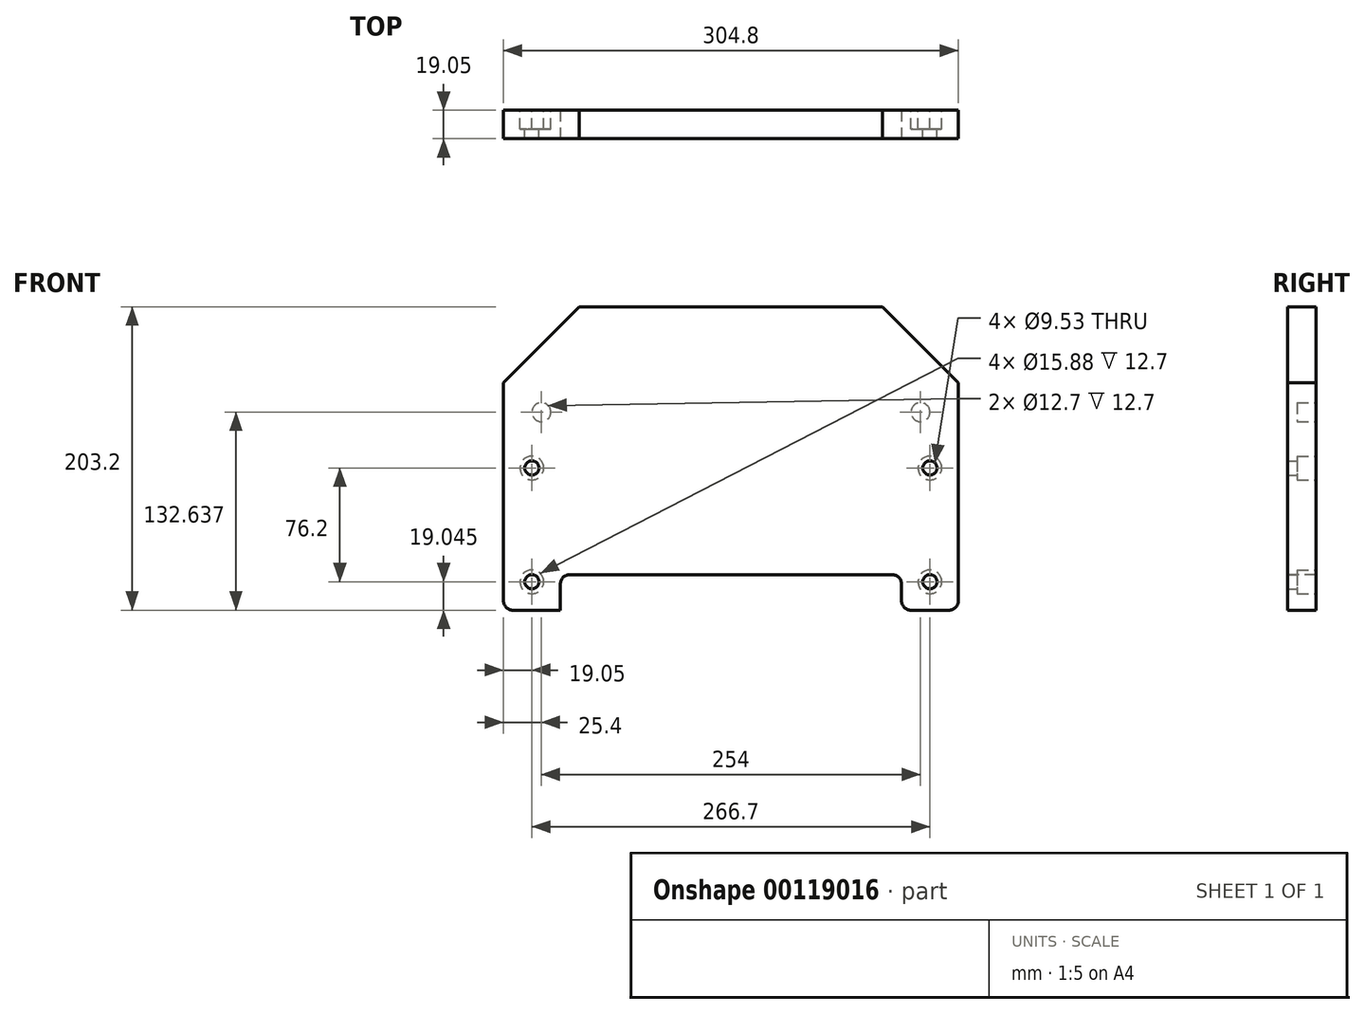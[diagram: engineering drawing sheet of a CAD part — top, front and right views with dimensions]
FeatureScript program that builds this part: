
annotation { "Feature Type Name" : "Feature", "Feature Type Description" : "" }
export const myFeature = defineFeature(function(context is Context, id is Id, definition is map)
    precondition{}
    {
        {
            var Q0;
            Q0=qCreatedBy(makeId("Front.planeOp"),FACE);
            var sketch = newSketch(context, id + "F0", { "sketchPlane" : qUnion([Q0])});
            skLineSegment(sketch, "E0.bottom", {"start": v(-194.83, 94.03) * mm, "end": v(109.97, 94.03) * mm});
            skLineSegment(sketch, "E0.top", {"start": v(-194.83, -109.17) * mm, "end": v(109.97, -109.17) * mm});
            skLineSegment(sketch, "E0.left", {"start": v(-194.83, 94.03) * mm, "end": v(-194.83, -109.17) * mm});
            skLineSegment(sketch, "E0.right", {"start": v(109.97, 94.03) * mm, "end": v(109.97, -109.17) * mm});
            skSolve(sketch);
        }
        {
            var Q0;
            Q0=makeQuery(id+"F0.imprint","IMPRINT",FACE,{"disambiguationData":[TD([[makeQuery(id+"F0.imprint","IMPRINT",EDGE,{"derivedFrom":sQuery(id+"F0.wireOp",EDGE,"E0.bottom")}),-1.0]])]});
            extrude(context, id + "F1", {"entities" : qUnion([Q0]), "depth" : 19.05 * mm});
        }
        {
            var Q0;
            Q0=makeQuery(id+"F1.opExtrude","CAP_FACE",FACE,{"disambiguationData":[OSD([sQuery(id+"F0.wireOp",EDGE,"E0.bottom"),sQuery(id+"F0.wireOp",EDGE,"E0.top"),sQuery(id+"F0.wireOp",EDGE,"E0.left"),sQuery(id+"F0.wireOp",EDGE,"E0.right")])],"isStart":false});
            var sketch = newSketch(context, id + "F2", { "sketchPlane" : qUnion([Q0])});
            skLineSegment(sketch, "E1.bottom", {"start": v(-156.73, -109.17) * mm, "end": v(71.87, -109.17) * mm});
            skLineSegment(sketch, "E1.top", {"start": v(-156.73, -85.32) * mm, "end": v(71.87, -85.32) * mm});
            skLineSegment(sketch, "E1.left", {"start": v(-156.73, -109.17) * mm, "end": v(-156.73, -85.32) * mm});
            skLineSegment(sketch, "E1.right", {"start": v(71.87, -109.17) * mm, "end": v(71.87, -85.32) * mm});
            skSolve(sketch);
        }
        {
            var Q0;
            Q0 = qSketchRegion(id + "F2", true);
            extrude(context, id + "F3", {"entities" : qUnion([Q0]), "operationType" : NewBodyOperationType.REMOVE, "endBound" : BoundingType.THROUGH_ALL, "oppositeDirection" : true, "depth" : 25.4 * mm});
        }
        {
            var Q0;
            Q0=makeQuery(id+"F3.boolean.opBoolean","COPY",EDGE,{"derivedFrom":makeQuery(id+"F3.opExtrude","SWEPT_EDGE",EDGE,{"disambiguationData":[OSD([sQuery(id+"F2.wireOp",EDGE,"E1.top"),sQuery(id+"F2.wireOp",EDGE,"E1.left")])]})});
            var Q1;
            Q1=makeQuery(id+"F3.boolean.opBoolean","COPY",EDGE,{"derivedFrom":makeQuery(id+"F3.opExtrude","SWEPT_EDGE",EDGE,{"disambiguationData":[OSD([sQuery(id+"F0.wireOp",EDGE,"E0.top"),sQuery(id+"F2.wireOp",EDGE,"E1.bottom"),sQuery(id+"F2.wireOp",EDGE,"E1.left")])]})});
            var Q2;
            Q2=makeQuery(id+"F1.opExtrude","SWEPT_EDGE",EDGE,{"disambiguationData":[OSD([sQuery(id+"F0.wireOp",EDGE,"E0.top"),sQuery(id+"F0.wireOp",EDGE,"E0.left")])]});
            var Q3;
            Q3=makeQuery(id+"F3.boolean.opBoolean","COPY",EDGE,{"derivedFrom":makeQuery(id+"F3.opExtrude","SWEPT_EDGE",EDGE,{"disambiguationData":[OSD([sQuery(id+"F2.wireOp",EDGE,"E1.top"),sQuery(id+"F2.wireOp",EDGE,"E1.right")])]})});
            var Q4;
            Q4=makeQuery(id+"F3.boolean.opBoolean","COPY",EDGE,{"derivedFrom":makeQuery(id+"F3.opExtrude","SWEPT_EDGE",EDGE,{"disambiguationData":[OSD([sQuery(id+"F0.wireOp",EDGE,"E0.top"),sQuery(id+"F2.wireOp",EDGE,"E1.bottom"),sQuery(id+"F2.wireOp",EDGE,"E1.right")])]})});
            var Q5;
            Q5=makeQuery(id+"F1.opExtrude","SWEPT_EDGE",EDGE,{"disambiguationData":[OSD([sQuery(id+"F0.wireOp",EDGE,"E0.top"),sQuery(id+"F0.wireOp",EDGE,"E0.right")])]});
            fillet(context, id + "F4", {"entities" : qUnion([Q0, Q1, Q2, Q3, Q4, Q5]), "radius" : 6.35 * mm, "tangentPropagation" : true, "allowEdgeOverflow" : false});
        }
        {
            var Q0;
            Q0=makeQuery(id+"F1.opExtrude","CAP_FACE",FACE,{"disambiguationData":[OSD([sQuery(id+"F0.wireOp",EDGE,"E0.bottom"),sQuery(id+"F0.wireOp",EDGE,"E0.top"),sQuery(id+"F0.wireOp",EDGE,"E0.left"),sQuery(id+"F0.wireOp",EDGE,"E0.right")])],"isStart":true});
            var sketch = newSketch(context, id + "F5", { "sketchPlane" : qUnion([Q0])});
            skPoint(sketch, "E2", {"position": v(42.43, -5.1) * mm});
            skPoint(sketch, "E2.positionSnap0", {"position": v(42.43, -85.32) * mm});
            skLineSegment(sketch, "E3", {"start": v(42.43, -5.1) * mm, "end": v(42.43, 23.47) * mm, "construction": true});
            skLineSegment(sketch, "E4", {"start": v(42.43, 23.47) * mm, "end": v(-84.57, 23.47) * mm});
            skLineSegment(sketch, "E5", {"start": v(42.43, 23.47) * mm, "end": v(169.43, 23.47) * mm});
            skCircle(sketch, "E6", {"center": v(169.43, 23.47) * mm, "radius": 6.35 * mm});
            skCircle(sketch, "E7", {"center": v(-84.57, 23.47) * mm, "radius": 6.35 * mm});
            skSolve(sketch);
        }
        {
            var Q0;
            Q0 = qSketchRegion(id + "F5", true);
            extrude(context, id + "F6", {"entities" : qUnion([Q0]), "operationType" : NewBodyOperationType.REMOVE, "oppositeDirection" : true, "depth" : 12.7 * mm});
        }
        {
            var Q0;
            Q0=makeQuery(id+"F1.opExtrude","CAP_FACE",FACE,{"disambiguationData":[OSD([sQuery(id+"F0.wireOp",EDGE,"E0.bottom"),sQuery(id+"F0.wireOp",EDGE,"E0.top"),sQuery(id+"F0.wireOp",EDGE,"E0.left"),sQuery(id+"F0.wireOp",EDGE,"E0.right")])],"isStart":true});
            var sketch = newSketch(context, id + "F7", { "sketchPlane" : qUnion([Q0])});
            skPoint(sketch, "E8", {"position": v(-90.92, -90.12) * mm});
            skPoint(sketch, "E8.positionSnap0", {"position": v(-90.92, -109.17) * mm});
            skPoint(sketch, "E9", {"position": v(-90.92, -13.92) * mm});
            skPoint(sketch, "E10", {"position": v(175.78, -90.12) * mm});
            skPoint(sketch, "E10.positionSnap0", {"position": v(175.78, -109.17) * mm});
            skPoint(sketch, "E11", {"position": v(175.78, -13.92) * mm});
            skSolve(sketch);
        }
        {
            var Q0;
            Q0=sQuery(id+"F7.wireOp",VERTEX,"E9");
            var Q1;
            Q1=sQuery(id+"F7.wireOp",VERTEX,"E8");
            var Q2;
            Q2=sQuery(id+"F7.wireOp",VERTEX,"E10");
            var Q3;
            Q3=sQuery(id+"F7.wireOp",VERTEX,"E11");
            var Q4;
            Q4=makeQuery(id+"F1.opExtrude","SWEPT_BODY",BODY,{"disambiguationData":[OSD([sQuery(id+"F0.wireOp",EDGE,"E0.bottom"),sQuery(id+"F0.wireOp",EDGE,"E0.top"),sQuery(id+"F0.wireOp",EDGE,"E0.left"),sQuery(id+"F0.wireOp",EDGE,"E0.right")])]});
            hole(context, id + "F8", {"style" : HoleStyle.C_BORE, "endStyle" : HoleEndStyle.THROUGH, "holeDiameter" : 9.52 * mm, "cBoreDiameter" : 15.88 * mm, "cBoreDepth" : 12.7 * mm, "locations" : qUnion([Q0, Q1, Q2, Q3]), "scope" : qUnion([Q4]), "isTappedThrough" : true});
        }
        {
            var Q0;
            Q0=makeQuery(id+"F1.opExtrude","SWEPT_EDGE",EDGE,{"disambiguationData":[OSD([sQuery(id+"F0.wireOp",EDGE,"E0.bottom"),sQuery(id+"F0.wireOp",EDGE,"E0.right")])]});
            var Q1;
            Q1=makeQuery(id+"F1.opExtrude","SWEPT_EDGE",EDGE,{"disambiguationData":[OSD([sQuery(id+"F0.wireOp",EDGE,"E0.bottom"),sQuery(id+"F0.wireOp",EDGE,"E0.left")])]});
            chamfer(context, id + "F9", {"entities" : qUnion([Q0, Q1]), "width" : 50.8 * mm, "tangentPropagation" : true});
        }
    });
